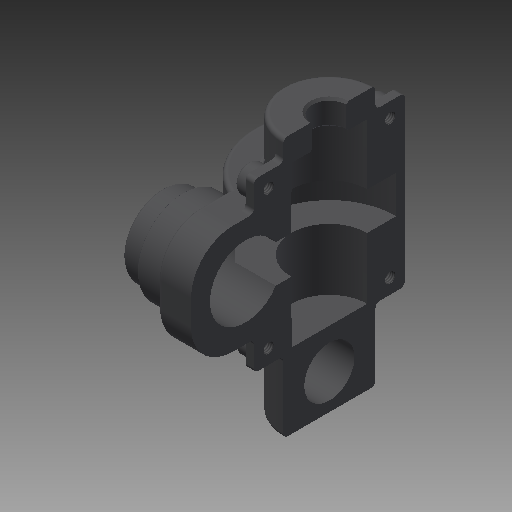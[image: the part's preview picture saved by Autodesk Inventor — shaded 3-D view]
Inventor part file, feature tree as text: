
AUTODESK INVENTOR PART (.ipt)
format: ipt  version: 2019 (Build 230136000, 136)  size: 435,200 bytes
history: native  units: mm
features: extrude x10, fillet x7, sketch x5, projected_geometry x2, plane x1, revolve x1, split x1, hole x1, chamfer x1
ambient origin geometry x8: Origin, YZ Plane, XZ Plane, XY Plane, X Axis, Y Axis, Z Axis, Center Point
bodies: Solid1 (feature_tree)
feature tree (29):
  extrude  "Extrusion1"  Depth=62.0mm TaperAngle=0.0deg
  plane  "Work Plane1"
  extrude  "Extrusion2"  Depth=36.0mm
  sketch  "Sketch3"  dims[d5=26.0mm d6=0.0mm d7=22.0mm]
  extrude  "Extrusion3"  Depth=22.0mm
  extrude  "Extrusion4"  Depth=15.0mm
  extrude  "Extrusion5"  Depth=1.0mm TaperAngle=0.0deg
  extrude  "Extrusion6"  Depth=1.0mm TaperAngle=0.0deg
  revolve  "Revolution1"  [1 undecoded]
  split  "Split1"
  extrude  "Extrusion7"  Depth=1.0mm
  extrude  "Extrusion8"  Depth=1.0mm TaperAngle=0.0deg
  fillet  "Fillet7"  Radius=34.0mm
  fillet  "Fillet8"  Radius=9.05mm
  fillet  "Fillet9"  Radius=9.0mm
  sketch  "Sketch5"  dims[d10=13.0mm d11=16.0mm d12=0.0mm d13=30.0mm d14=0.0mm d15=19.0mm d16=17.0mm d17=40.0mm d18=0.0mm d19=34.0mm d20=0.0mm d25=9.05mm d26=9.0mm d28=6.0mm d29=4.05mm d30=2.0mm d31=14.65mm d32=90.0deg d34=12.0mm d35=8.374731mm d36=56.0mm d37=0.0mm d40=10.0mm d41=56.0mm d42=0.0mm d47=10.0mm d48=1.0mm d49=0.5mm d51=7.0mm d52=7.0mm d53=3.5mm d54=3.5mm d56=2.0mm d57=0.0mm d67=26.0mm d78=6.5mm d79=6.5mm d80=6.5mm d81=6.5mm d82=5.0mm d83=0.0mm d84=2.459mm d85=6.0mm d86=6.3mm d87=2.0mm d88=90.0deg d89=4.0mm d90=20.594885mm d91=2.0mm d92=0.5mm d93=2.0mm d94=45.0deg d95=1.0mm d96=1.0mm d97=1.0mm d98=1.0mm d99=0.625269mm]
  extrude  "Extrusion9"  Depth=1.0mm
  extrude  "Extrusion11"  Depth=1.0mm
  hole  "Hole2"  [1 undecoded]
  chamfer  "Chamfer1"  Distance=14.65mm
  fillet  "Fillet13"  [1 undecoded]
  fillet  "Fillet14"  Radius=12.0mm
  fillet  "Fillet15"  Radius=8.374731mm
  fillet  "Fillet16"  Radius=56.0mm
  sketch  "Sketch1"  dims[d0=22.0mm d1=62.0mm d2=0.0mm]
  sketch  "Sketch2"  dims[d3=-24.0mm d4=36.0mm]
  sketch  "Sketch4"  dims[d8=20.0mm d9=15.0mm]
  projected_geometry  "Project Cut Edges1"
  projected_geometry  "Project Cut Edges2"
note: 3 required parameter values undecoded (feature->parameter linkage not recoverable at this tier; creation-order binding heuristic only, values carry confidence <= 0.55)